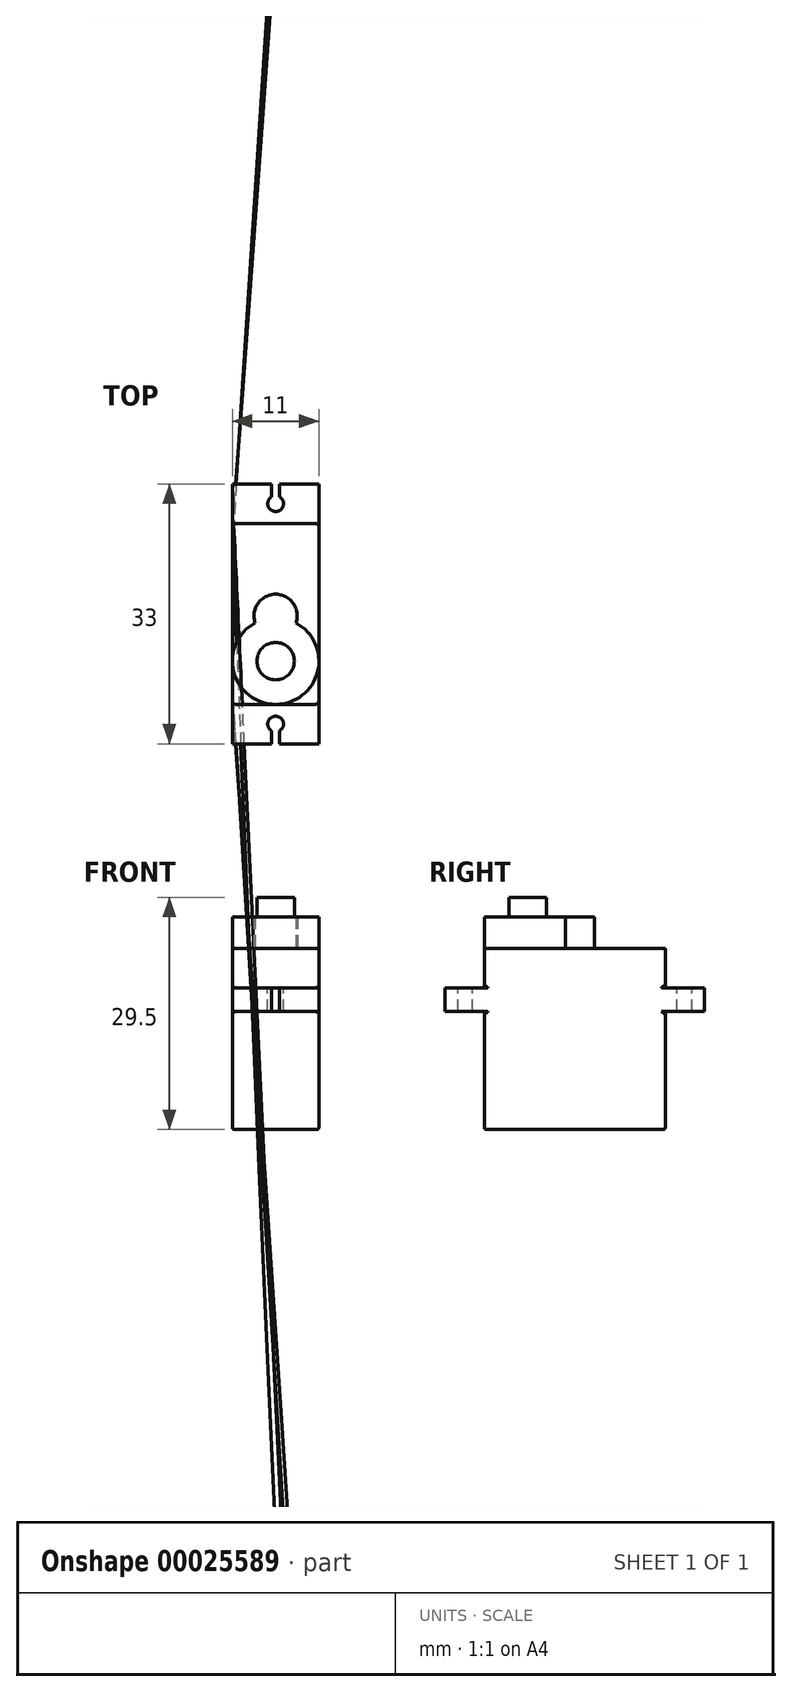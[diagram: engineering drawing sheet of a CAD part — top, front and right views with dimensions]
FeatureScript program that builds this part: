
annotation { "Feature Type Name" : "Feature", "Feature Type Description" : "" }
export const myFeature = defineFeature(function(context is Context, id is Id, definition is map)
    precondition{}
    {
        {
            var Q0;
            Q0=qCreatedBy(makeId("Top.planeOp"),FACE);
            var sketch = newSketch(context, id + "F7", { "sketchPlane" : qUnion([Q0])});
            skLineSegment(sketch, "E0.bottom", {"start": v(0, 0) * mm, "end": v(11, 0) * mm});
            skLineSegment(sketch, "E0.top", {"start": v(0, 23) * mm, "end": v(11, 23) * mm});
            skLineSegment(sketch, "E0.left", {"start": v(0, 0) * mm, "end": v(0, 23) * mm});
            skLineSegment(sketch, "E0.right", {"start": v(11, 0) * mm, "end": v(11, 23) * mm});
            skSolve(sketch);
        }
        {
            var Q0;
            Q0=makeQuery(id+"F7.imprint","IMPRINT",FACE,{"disambiguationData":[TD([[makeQuery(id+"F7.imprint","IMPRINT",EDGE,{"derivedFrom":sQuery(id+"F7.wireOp",EDGE,"E0.bottom")}),1.0]])]});
            extrude(context, id + "F0", {"entities" : qUnion([Q0]), "oppositeDirection" : true, "depth" : 23 * mm});
        }
        {
            var Q0;
            Q0=qCreatedBy(makeId("Top.planeOp"),FACE);
            cPlane(context, id + "F1", {"entities" : qUnion([Q0]), "cplaneType" : CPlaneType.OFFSET, "offset" : 5 * mm, "oppositeDirection" : true, "width" : 150 * mm, "height" : 150 * mm});
        }
        {
            var Q0;
            Q0=qCreatedBy(id+"F1.planeOp",FACE);
            var sketch = newSketch(context, id + "F8", { "sketchPlane" : qUnion([Q0])});
            skLineSegment(sketch, "E1.bottom", {"start": v(0, -5) * mm, "end": v(5, -5) * mm});
            skLineSegment(sketch, "E1.top", {"start": v(0, 28) * mm, "end": v(5, 28) * mm});
            skLineSegment(sketch, "E1.left", {"start": v(0, -5) * mm, "end": v(0, 28) * mm});
            skLineSegment(sketch, "E1.right", {"start": v(11, -5) * mm, "end": v(11, 28) * mm});
            skLineSegment(sketch, "E2.0", {"start": v(0, 0) * mm, "end": v(11, 0) * mm, "construction": true});
            skLineSegment(sketch, "E3.0", {"start": v(0, 23) * mm, "end": v(11, 23) * mm, "construction": true});
            skLineSegment(sketch, "E4", {"start": v(5.5, 28) * mm, "end": v(5.5, 25.5) * mm, "construction": true});
            skLineSegment(sketch, "E5", {"start": v(5.5, -5) * mm, "end": v(5.5, -2.5) * mm, "construction": true});
            skArc(sketch, "E6", {"start": v(5, 26.37) * mm, "mid": v(5.5, 24.5) * mm, "end": v(6, 26.37) * mm});
            skArc(sketch, "E7", {"start": v(6, -3.37) * mm, "mid": v(5.5, -1.5) * mm, "end": v(5, -3.37) * mm});
            skLineSegment(sketch, "E8", {"start": v(5, -5) * mm, "end": v(5, -3.37) * mm});
            skLineSegment(sketch, "E9", {"start": v(6, -5) * mm, "end": v(6, -3.37) * mm});
            skLineSegment(sketch, "E10", {"start": v(5, 28) * mm, "end": v(5, 26.37) * mm});
            skLineSegment(sketch, "E11", {"start": v(6, 28) * mm, "end": v(6, 26.37) * mm});
            skLineSegment(sketch, "E12.trimOffspring", {"start": v(6, -5) * mm, "end": v(11, -5) * mm});
            skLineSegment(sketch, "E13.trimOffspring", {"start": v(6, 28) * mm, "end": v(11, 28) * mm});
            skSolve(sketch);
        }
        {
            var Q0;
            Q0=makeQuery(id+"F8.imprint","IMPRINT",FACE,{"disambiguationData":[TD([[makeQuery(id+"F8.imprint","IMPRINT",EDGE,{"derivedFrom":sQuery(id+"F8.wireOp",EDGE,"E1.bottom")}),1.0]])]});
            extrude(context, id + "F9", {"entities" : qUnion([Q0]), "operationType" : NewBodyOperationType.ADD, "oppositeDirection" : true, "depth" : 3 * mm});
        }
        {
            var Q0;
            Q0=makeQuery(id+"F0.opExtrude","CAP_FACE",FACE,{"disambiguationData":[OSD([sQuery(id+"F7.wireOp",EDGE,"E0.bottom"),sQuery(id+"F7.wireOp",EDGE,"E0.top"),sQuery(id+"F7.wireOp",EDGE,"E0.left"),sQuery(id+"F7.wireOp",EDGE,"E0.right")])],"isStart":true});
            var sketch = newSketch(context, id + "F2", { "sketchPlane" : qUnion([Q0])});
            skLineSegment(sketch, "E14", {"start": v(5.5, 5.5) * mm, "end": v(5.5, 0) * mm, "construction": true});
            skArc(sketch, "E15", {"start": v(2.9, 10.35) * mm, "mid": v(5.5, 0) * mm, "end": v(8.1, 10.35) * mm});
            skLineSegment(sketch, "E16", {"start": v(5.5, 5.5) * mm, "end": v(5.5, 11.25) * mm, "construction": true});
            skArc(sketch, "E17", {"start": v(8.1, 10.35) * mm, "mid": v(5.5, 14) * mm, "end": v(2.9, 10.35) * mm});
            skSolve(sketch);
        }
        {
            var Q0;
            Q0=makeQuery(id+"F2.imprint","IMPRINT",FACE,{"disambiguationData":[TD([[makeQuery(id+"F2.imprint","IMPRINT",EDGE,{"derivedFrom":sQuery(id+"F2.wireOp",EDGE,"E15")}),1.0]])]});
            extrude(context, id + "F10", {"entities" : qUnion([Q0]), "operationType" : NewBodyOperationType.ADD, "depth" : 4 * mm});
        }
        {
            var Q0;
            Q0=makeQuery(id+"F10.opExtrude","CAP_FACE",FACE,{"disambiguationData":[OSD([sQuery(id+"F2.wireOp",EDGE,"E15"),sQuery(id+"F2.wireOp",EDGE,"E17")])],"isStart":false});
            var sketch = newSketch(context, id + "F3", { "sketchPlane" : qUnion([Q0])});
            skCircle(sketch, "E18", {"center": v(5.5, 5.5) * mm, "radius": 2.38 * mm});
            skSolve(sketch);
        }
        {
            var Q0;
            Q0=makeQuery(id+"F3.imprint","IMPRINT",FACE,{"disambiguationData":[TD([[makeQuery(id+"F3.imprint","IMPRINT",EDGE,{"derivedFrom":sQuery(id+"F3.wireOp",EDGE,"E18")}),1.0]])]});
            extrude(context, id + "F4", {"entities" : qUnion([Q0]), "depth" : 2.5 * mm});
        }
        {
            var Q0;
            {var subQ0=sQuery(id+"F7.wireOp",EDGE,"E0.bottom");var subQ1=sQuery(id+"F7.wireOp",EDGE,"E0.right");Q0=makeQuery(id+"F9.boolean.opBoolean","SPLIT",EDGE,{"disambiguationData":[TD([makeQuery(id+"F0.opExtrude","CAP_FACE",FACE,{"disambiguationData":[OSD([subQ0,sQuery(id+"F7.wireOp",EDGE,"E0.top"),sQuery(id+"F7.wireOp",EDGE,"E0.left"),subQ1])],"isStart":true})])],"derivedFrom":makeQuery(id+"F0.opExtrude","SWEPT_EDGE",EDGE,{"disambiguationData":[OSD([subQ0,subQ1])]})});}
            var Q1;
            {var subQ0=sQuery(id+"F7.wireOp",EDGE,"E0.bottom");var subQ1=sQuery(id+"F7.wireOp",EDGE,"E0.right");Q1=makeQuery(id+"F9.boolean.opBoolean","SPLIT",EDGE,{"disambiguationData":[TD([makeQuery(id+"F0.opExtrude","CAP_FACE",FACE,{"disambiguationData":[OSD([subQ0,sQuery(id+"F7.wireOp",EDGE,"E0.top"),sQuery(id+"F7.wireOp",EDGE,"E0.left"),subQ1])],"isStart":false})])],"derivedFrom":makeQuery(id+"F0.opExtrude","SWEPT_EDGE",EDGE,{"disambiguationData":[OSD([subQ0,subQ1])]})});}
            var Q2;
            {var subQ0=sQuery(id+"F7.wireOp",EDGE,"E0.bottom");var subQ1=sQuery(id+"F7.wireOp",EDGE,"E0.left");Q2=makeQuery(id+"F9.boolean.opBoolean","SPLIT",EDGE,{"disambiguationData":[TD([makeQuery(id+"F0.opExtrude","CAP_FACE",FACE,{"disambiguationData":[OSD([subQ0,sQuery(id+"F7.wireOp",EDGE,"E0.top"),subQ1,sQuery(id+"F7.wireOp",EDGE,"E0.right")])],"isStart":false})])],"derivedFrom":makeQuery(id+"F0.opExtrude","SWEPT_EDGE",EDGE,{"disambiguationData":[OSD([subQ0,subQ1])]})});}
            var Q3;
            {var subQ0=sQuery(id+"F7.wireOp",EDGE,"E0.bottom");var subQ1=sQuery(id+"F7.wireOp",EDGE,"E0.left");Q3=makeQuery(id+"F9.boolean.opBoolean","SPLIT",EDGE,{"disambiguationData":[TD([makeQuery(id+"F0.opExtrude","CAP_FACE",FACE,{"disambiguationData":[OSD([subQ0,sQuery(id+"F7.wireOp",EDGE,"E0.top"),subQ1,sQuery(id+"F7.wireOp",EDGE,"E0.right")])],"isStart":true})])],"derivedFrom":makeQuery(id+"F0.opExtrude","SWEPT_EDGE",EDGE,{"disambiguationData":[OSD([subQ0,subQ1])]})});}
            var Q4;
            {var subQ0=sQuery(id+"F7.wireOp",EDGE,"E0.top");var subQ1=sQuery(id+"F7.wireOp",EDGE,"E0.right");Q4=makeQuery(id+"F9.boolean.opBoolean","SPLIT",EDGE,{"disambiguationData":[TD([makeQuery(id+"F0.opExtrude","CAP_FACE",FACE,{"disambiguationData":[OSD([sQuery(id+"F7.wireOp",EDGE,"E0.bottom"),subQ0,sQuery(id+"F7.wireOp",EDGE,"E0.left"),subQ1])],"isStart":true})])],"derivedFrom":makeQuery(id+"F0.opExtrude","SWEPT_EDGE",EDGE,{"disambiguationData":[OSD([subQ0,subQ1])]})});}
            var Q5;
            {var subQ0=sQuery(id+"F7.wireOp",EDGE,"E0.top");var subQ1=sQuery(id+"F7.wireOp",EDGE,"E0.right");Q5=makeQuery(id+"F9.boolean.opBoolean","SPLIT",EDGE,{"disambiguationData":[TD([makeQuery(id+"F0.opExtrude","CAP_FACE",FACE,{"disambiguationData":[OSD([sQuery(id+"F7.wireOp",EDGE,"E0.bottom"),subQ0,sQuery(id+"F7.wireOp",EDGE,"E0.left"),subQ1])],"isStart":false})])],"derivedFrom":makeQuery(id+"F0.opExtrude","SWEPT_EDGE",EDGE,{"disambiguationData":[OSD([subQ0,subQ1])]})});}
            var Q6;
            {var subQ0=sQuery(id+"F7.wireOp",EDGE,"E0.top");var subQ1=sQuery(id+"F7.wireOp",EDGE,"E0.left");Q6=makeQuery(id+"F9.boolean.opBoolean","SPLIT",EDGE,{"disambiguationData":[TD([makeQuery(id+"F0.opExtrude","CAP_FACE",FACE,{"disambiguationData":[OSD([sQuery(id+"F7.wireOp",EDGE,"E0.bottom"),subQ0,subQ1,sQuery(id+"F7.wireOp",EDGE,"E0.right")])],"isStart":false})])],"derivedFrom":makeQuery(id+"F0.opExtrude","SWEPT_EDGE",EDGE,{"disambiguationData":[OSD([subQ0,subQ1])]})});}
            var Q7;
            {var subQ0=sQuery(id+"F7.wireOp",EDGE,"E0.top");var subQ1=sQuery(id+"F7.wireOp",EDGE,"E0.left");Q7=makeQuery(id+"F9.boolean.opBoolean","SPLIT",EDGE,{"disambiguationData":[TD([makeQuery(id+"F0.opExtrude","CAP_FACE",FACE,{"disambiguationData":[OSD([sQuery(id+"F7.wireOp",EDGE,"E0.bottom"),subQ0,subQ1,sQuery(id+"F7.wireOp",EDGE,"E0.right")])],"isStart":true})])],"derivedFrom":makeQuery(id+"F0.opExtrude","SWEPT_EDGE",EDGE,{"disambiguationData":[OSD([subQ0,subQ1])]})});}
            fillet(context, id + "F5", {"entities" : qUnion([Q0, Q1, Q2, Q3, Q4, Q5, Q6, Q7]), "radius" : 0.5 * mm, "allowEdgeOverflow" : false});
        }
        {
            var Q0;
            Q0=makeQuery(id+"F9.boolean.opBoolean","INTERSECT",EDGE,{"derivedFrom":[makeQuery(id+"F0.opExtrude","SWEPT_FACE",FACE,{"disambiguationData":[OSD([sQuery(id+"F7.wireOp",EDGE,"E0.bottom")])]}),makeQuery(id+"F9.opExtrude","CAP_FACE",FACE,{"disambiguationData":[OSD([sQuery(id+"F8.wireOp",EDGE,"E1.bottom"),sQuery(id+"F8.wireOp",EDGE,"E1.top"),sQuery(id+"F8.wireOp",EDGE,"E1.left"),sQuery(id+"F8.wireOp",EDGE,"E1.right"),sQuery(id+"F8.wireOp",EDGE,"E6"),sQuery(id+"F8.wireOp",EDGE,"E7"),sQuery(id+"F8.wireOp",EDGE,"E8"),sQuery(id+"F8.wireOp",EDGE,"E9"),sQuery(id+"F8.wireOp",EDGE,"E10"),sQuery(id+"F8.wireOp",EDGE,"E11"),sQuery(id+"F8.wireOp",EDGE,"E12.trimOffspring"),sQuery(id+"F8.wireOp",EDGE,"E13.trimOffspring")])],"isStart":true})]});
            var Q1;
            Q1=makeQuery(id+"F9.boolean.opBoolean","INTERSECT",EDGE,{"derivedFrom":[makeQuery(id+"F0.opExtrude","SWEPT_FACE",FACE,{"disambiguationData":[OSD([sQuery(id+"F7.wireOp",EDGE,"E0.bottom")])]}),makeQuery(id+"F9.opExtrude","CAP_FACE",FACE,{"disambiguationData":[OSD([sQuery(id+"F8.wireOp",EDGE,"E1.bottom"),sQuery(id+"F8.wireOp",EDGE,"E1.top"),sQuery(id+"F8.wireOp",EDGE,"E1.left"),sQuery(id+"F8.wireOp",EDGE,"E1.right"),sQuery(id+"F8.wireOp",EDGE,"E6"),sQuery(id+"F8.wireOp",EDGE,"E7"),sQuery(id+"F8.wireOp",EDGE,"E8"),sQuery(id+"F8.wireOp",EDGE,"E9"),sQuery(id+"F8.wireOp",EDGE,"E10"),sQuery(id+"F8.wireOp",EDGE,"E11"),sQuery(id+"F8.wireOp",EDGE,"E12.trimOffspring"),sQuery(id+"F8.wireOp",EDGE,"E13.trimOffspring")])],"isStart":false})]});
            var Q2;
            Q2=makeQuery(id+"F9.boolean.opBoolean","INTERSECT",EDGE,{"derivedFrom":[makeQuery(id+"F0.opExtrude","SWEPT_FACE",FACE,{"disambiguationData":[OSD([sQuery(id+"F7.wireOp",EDGE,"E0.top")])]}),makeQuery(id+"F9.opExtrude","CAP_FACE",FACE,{"disambiguationData":[OSD([sQuery(id+"F8.wireOp",EDGE,"E1.bottom"),sQuery(id+"F8.wireOp",EDGE,"E1.top"),sQuery(id+"F8.wireOp",EDGE,"E1.left"),sQuery(id+"F8.wireOp",EDGE,"E1.right"),sQuery(id+"F8.wireOp",EDGE,"E6"),sQuery(id+"F8.wireOp",EDGE,"E7"),sQuery(id+"F8.wireOp",EDGE,"E8"),sQuery(id+"F8.wireOp",EDGE,"E9"),sQuery(id+"F8.wireOp",EDGE,"E10"),sQuery(id+"F8.wireOp",EDGE,"E11"),sQuery(id+"F8.wireOp",EDGE,"E12.trimOffspring"),sQuery(id+"F8.wireOp",EDGE,"E13.trimOffspring")])],"isStart":true})]});
            var Q3;
            Q3=makeQuery(id+"F9.boolean.opBoolean","INTERSECT",EDGE,{"derivedFrom":[makeQuery(id+"F0.opExtrude","SWEPT_FACE",FACE,{"disambiguationData":[OSD([sQuery(id+"F7.wireOp",EDGE,"E0.top")])]}),makeQuery(id+"F9.opExtrude","CAP_FACE",FACE,{"disambiguationData":[OSD([sQuery(id+"F8.wireOp",EDGE,"E1.bottom"),sQuery(id+"F8.wireOp",EDGE,"E1.top"),sQuery(id+"F8.wireOp",EDGE,"E1.left"),sQuery(id+"F8.wireOp",EDGE,"E1.right"),sQuery(id+"F8.wireOp",EDGE,"E6"),sQuery(id+"F8.wireOp",EDGE,"E7"),sQuery(id+"F8.wireOp",EDGE,"E8"),sQuery(id+"F8.wireOp",EDGE,"E9"),sQuery(id+"F8.wireOp",EDGE,"E10"),sQuery(id+"F8.wireOp",EDGE,"E11"),sQuery(id+"F8.wireOp",EDGE,"E12.trimOffspring"),sQuery(id+"F8.wireOp",EDGE,"E13.trimOffspring")])],"isStart":false})]});
            var Q4;
            {var subQ0=sQuery(id+"F2.wireOp",EDGE,"E15");var subQ1=sQuery(id+"F7.wireOp",EDGE,"E0.right");Q4=makeQuery(id+"F10.boolean.opBoolean","SPLIT",EDGE,{"disambiguationData":[TD([makeQuery(id+"F0.opExtrude","CAP_FACE",FACE,{"disambiguationData":[OSD([sQuery(id+"F7.wireOp",EDGE,"E0.bottom"),sQuery(id+"F7.wireOp",EDGE,"E0.top"),sQuery(id+"F7.wireOp",EDGE,"E0.left"),subQ1])],"isStart":true}),makeQuery(id+"F0.opExtrude","SWEPT_FACE",FACE,{"disambiguationData":[OSD([subQ1])]}),makeQuery(id+"F9.opExtrude","SWEPT_FACE",FACE,{"disambiguationData":[OSD([sQuery(id+"F8.wireOp",EDGE,"E1.right")])]}),makeQuery(id+"F10.opExtrude","SWEPT_FACE",FACE,{"disambiguationData":[OSD([subQ0])]}),makeQuery(id+"F10.opExtrude","SWEPT_FACE",FACE,{"disambiguationData":[OSD([sQuery(id+"F2.wireOp",EDGE,"E17")])]})])],"derivedFrom":makeQuery(id+"F10.opExtrude","CAP_EDGE",EDGE,{"disambiguationData":[OSD([subQ0])],"isStart":true})});}
            var Q5;
            Q5=makeQuery(id+"F10.opExtrude","CAP_EDGE",EDGE,{"disambiguationData":[OSD([sQuery(id+"F2.wireOp",EDGE,"E17")])],"isStart":true});
            var Q6;
            Q6=makeQuery(id+"F0.opExtrude","CAP_FACE",FACE,{"disambiguationData":[OSD([sQuery(id+"F7.wireOp",EDGE,"E0.bottom"),sQuery(id+"F7.wireOp",EDGE,"E0.top"),sQuery(id+"F7.wireOp",EDGE,"E0.left"),sQuery(id+"F7.wireOp",EDGE,"E0.right")])],"isStart":false});
            fillet(context, id + "F6", {"entities" : qUnion([Q0, Q1, Q2, Q3, Q4, Q5, Q6]), "radius" : 0.25 * mm, "tangentPropagation" : true, "allowEdgeOverflow" : false});
        }
    });
